# Revit family: Luminaria ELIUM
name_source: partatom
category: Luminarias
revit_build: Autodesk Revit 2016 (Build: 20150220_1215(x64)
units: mm (PartAtom-declared; Revit-internal decimal feet)

## family parameters
Compartido = No
Corte con vacíos al cargar = No
Cota de conector redondo = Diámetro de uso
Número OmniClass = 23.80.70.00
Origen de luz = Sí
Punto de cálculo de habitación = No
Se basa en plano de trabajo = No
Siempre vertical = No
Tipo de pieza = Normal
Título OmniClass = Lighting

## types (1)
- ELIUM M 64 LED G3 700 mA 136W 4000K T4Z
    Altura columna = 4-12 m
    Ancho = 310 mm  [stored 1.01706 ft]
    Anchura rectángulo de emisión = 275 mm
    Archivo de red fotométrica = ILLI06444Z_ELIUM64LEDG3700mA136W4000KT4Z-15950.ies
    Cambio de temperatura de color de luz atenuada = <Ninguno>
    Carga aparente = 0 VA
    Certificaciones = CE, ENEC, AENOR, CB SCHEME, RETILAP
    Clase de aislamiento = Clase I / Clase II
    Classificación = Iluminación
    Comentarios de tipo = Elium es una luminaria de diseño extra plano con una extraordinaria relación entre eficiencia y coste. Concebida para aplicaciones tipo vial pero tamibién útil en multitud de aplicaciones.
    Comentarios de vataje = 1
    Descripción = Diseño aerodinámico. Excelente disipación térmica.Disipación pasiva sin aletas.Minima superficie de resistencia al aire.Diesño con antideslumbramiento.
    Diametro fijación = Ø 60 mm tanto en top como en lateral
    Difusor = Cristal plano
    Driver = Incluido
    Fabricante = BENITO
    Ficha tecnica = http://www.benito.com
    Filtro de color = 16777215
    Forma visible en renderización = No
    Frequencia nominal = 50/60Hz
    Inclinación = -15°,-10°,-5°,0°,5°,10°y 15°
    Instrucciones de montaje = http://www.benito.com
    Largo = 610 mm  [stored 2.00131 ft]
    Longitud de rectángulo de emisión = 240 mm  [stored 0.787402 ft]
    Lámpara = Led
    Material cuerpo = Inyección Aluminio
    Modelo = ELIUM M 64 LED G3 700 mA 136W 4000K T4Z
    Peso = 7,2 Kg
    Protección IP = 66
    Protección impacto IK = 08
    Referencia = ILLI
    Regulable = Si
    Sistema regulable = Si
    Tipo de opticas = T1, T3, T9
    URL = http://www.benito.com
    URL producto = http://www.benito.com
    Voltage nominal = 220/240 V
    Ángulo de inclinación = 90.00°

note: [stored X ft] marks values corroborated as IEEE doubles in the binary element streams (Revit-internal decimal feet)
